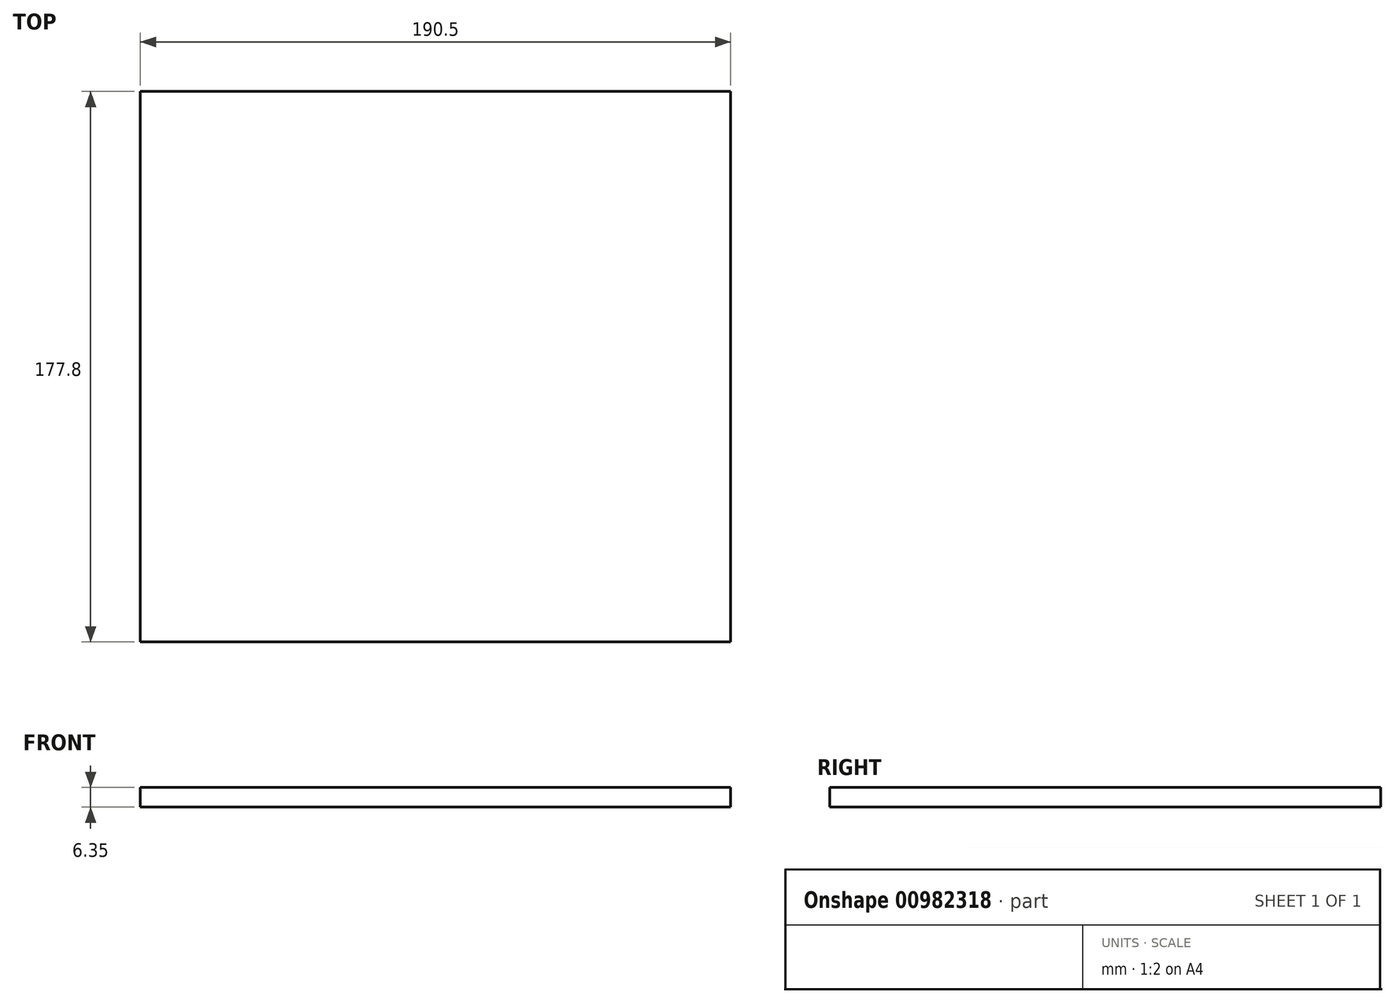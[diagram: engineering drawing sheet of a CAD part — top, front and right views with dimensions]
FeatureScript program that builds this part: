
annotation { "Feature Type Name" : "Feature", "Feature Type Description" : "" }
export const myFeature = defineFeature(function(context is Context, id is Id, definition is map)
    precondition{}
    {
        {
            var Q0;
            Q0=qCreatedBy(makeId("Top.planeOp"),FACE);
            var sketch = newSketch(context, id + "F0", { "sketchPlane" : qUnion([Q0])});
            skLineSegment(sketch, "E0.bottom", {"start": v(0, 0) * mm, "end": v(190.5, 0) * mm});
            skLineSegment(sketch, "E0.top", {"start": v(0, 177.8) * mm, "end": v(190.5, 177.8) * mm});
            skLineSegment(sketch, "E0.left", {"start": v(0, 0) * mm, "end": v(0, 177.8) * mm});
            skLineSegment(sketch, "E0.right", {"start": v(190.5, 0) * mm, "end": v(190.5, 177.8) * mm});
            skSolve(sketch);
        }
        {
            var Q0;
            Q0 = qSketchRegion(id + "F0", true);
            extrude(context, id + "F1", {"entities" : qUnion([Q0]), "depth" : 6.35 * mm, "offsetDistance" : 25.4 * mm});
        }
    });
